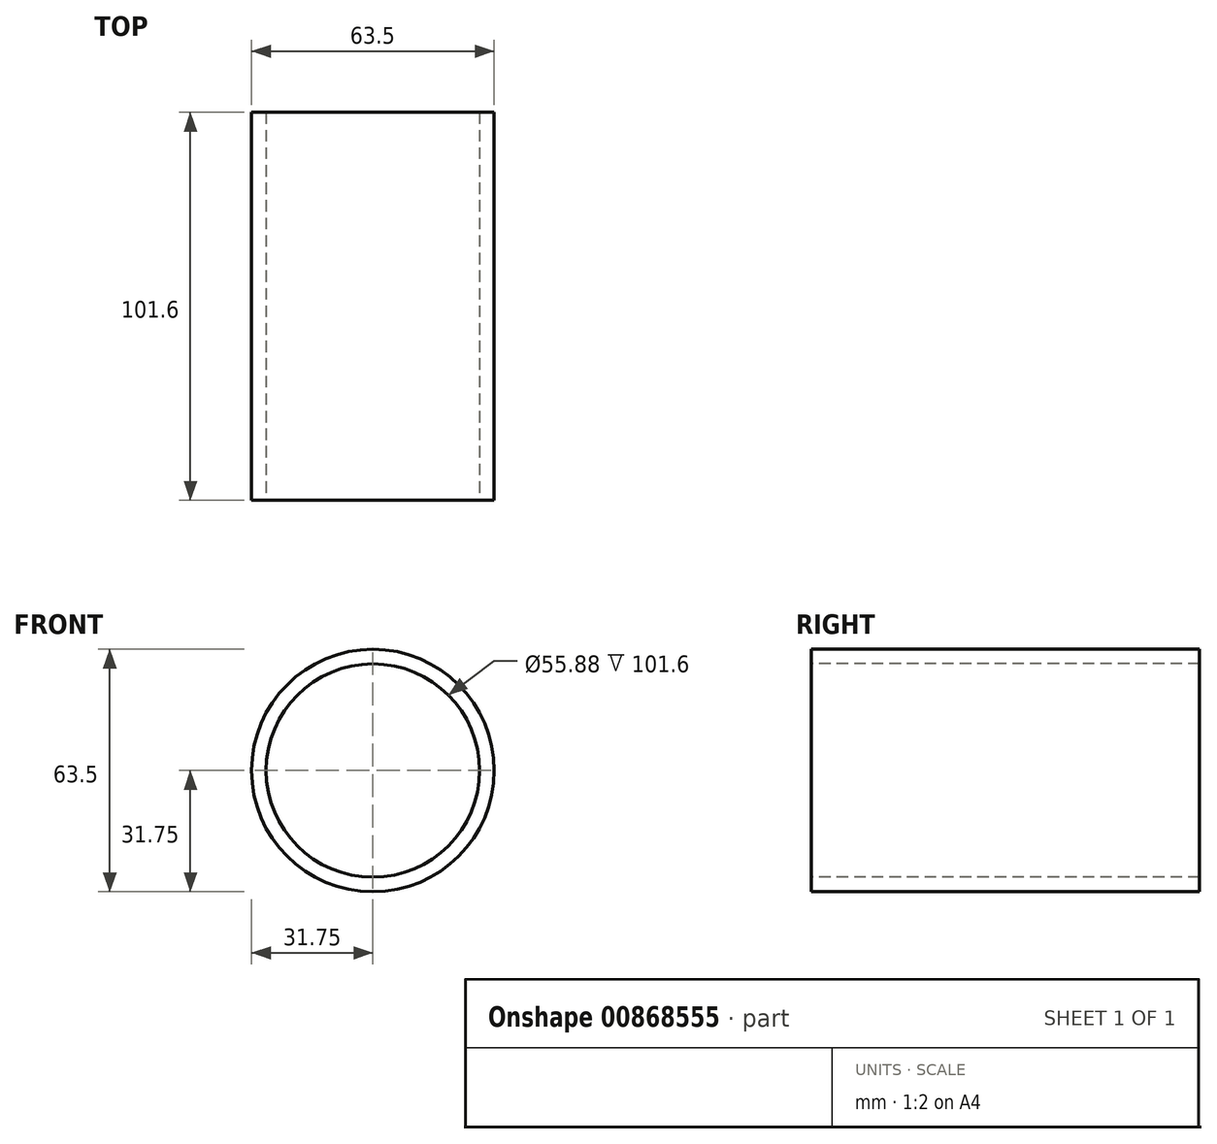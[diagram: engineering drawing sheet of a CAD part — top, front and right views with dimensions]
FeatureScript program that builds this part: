
annotation { "Feature Type Name" : "Feature", "Feature Type Description" : "" }
export const myFeature = defineFeature(function(context is Context, id is Id, definition is map)
    precondition{}
    {
        {
            var Q0;
            Q0=qCreatedBy(makeId("Front.planeOp"),FACE);
            var sketch = newSketch(context, id + "F0", { "sketchPlane" : qUnion([Q0])});
            skCircle(sketch, "E0", {"center": v(0, 0) * mm, "radius": 31.75 * mm});
            skSolve(sketch);
        }
        {
            var Q0;
            Q0 = qSketchRegion(id + "F0", true);
            extrude(context, id + "F1", {"entities" : qUnion([Q0]), "oppositeDirection" : true, "depth" : 50.8 * mm, "offsetDistance" : 25.4 * mm});
        }
        {
            var Q0;
            Q0=makeQuery(id+"F1.opExtrude","CAP_FACE",FACE,{"disambiguationData":[OSD([sQuery(id+"F0.wireOp",EDGE,"E0")])],"isStart":true});
            extrude(context, id + "F2", {"entities" : qUnion([Q0]), "operationType" : NewBodyOperationType.ADD, "depth" : 50.8 * mm, "offsetDistance" : 25.4 * mm});
        }
        {
            var Q0;
            Q0=qCreatedBy(makeId("Front.planeOp"),FACE);
            var sketch = newSketch(context, id + "F3", { "sketchPlane" : qUnion([Q0])});
            skCircle(sketch, "E1", {"center": v(0, 0) * mm, "radius": 27.94 * mm});
            skSolve(sketch);
        }
        {
            var Q0;
            Q0 = qSketchRegion(id + "F3", true);
            extrude(context, id + "F4", {"entities" : qUnion([Q0]), "operationType" : NewBodyOperationType.REMOVE, "oppositeDirection" : true, "depth" : 50.8 * mm, "offsetDistance" : 25.4 * mm});
        }
        {
            var Q0;
            Q0=makeQuery(id+"F4.boolean.opBoolean","COPY",FACE,{"derivedFrom":makeQuery(id+"F4.opExtrude","CAP_FACE",FACE,{"disambiguationData":[OSD([sQuery(id+"F3.wireOp",EDGE,"E1")])],"isStart":true})});
            extrude(context, id + "F5", {"entities" : qUnion([Q0]), "operationType" : NewBodyOperationType.REMOVE, "oppositeDirection" : true, "depth" : 50.8 * mm, "offsetDistance" : 25.4 * mm});
        }
        {
            var Q0;
            Q0=qCreatedBy(makeId("Top.planeOp"),FACE);
            var sketch = newSketch(context, id + "F6", { "sketchPlane" : qUnion([Q0])});
            skPoint(sketch, "E2", {"position": v(0, 61.91) * mm});
            skPoint(sketch, "E3", {"position": v(-29.49, 76.36) * mm});
            skPoint(sketch, "E4", {"position": v(10.27, 61.91) * mm});
            skSolve(sketch);
        }
    });
